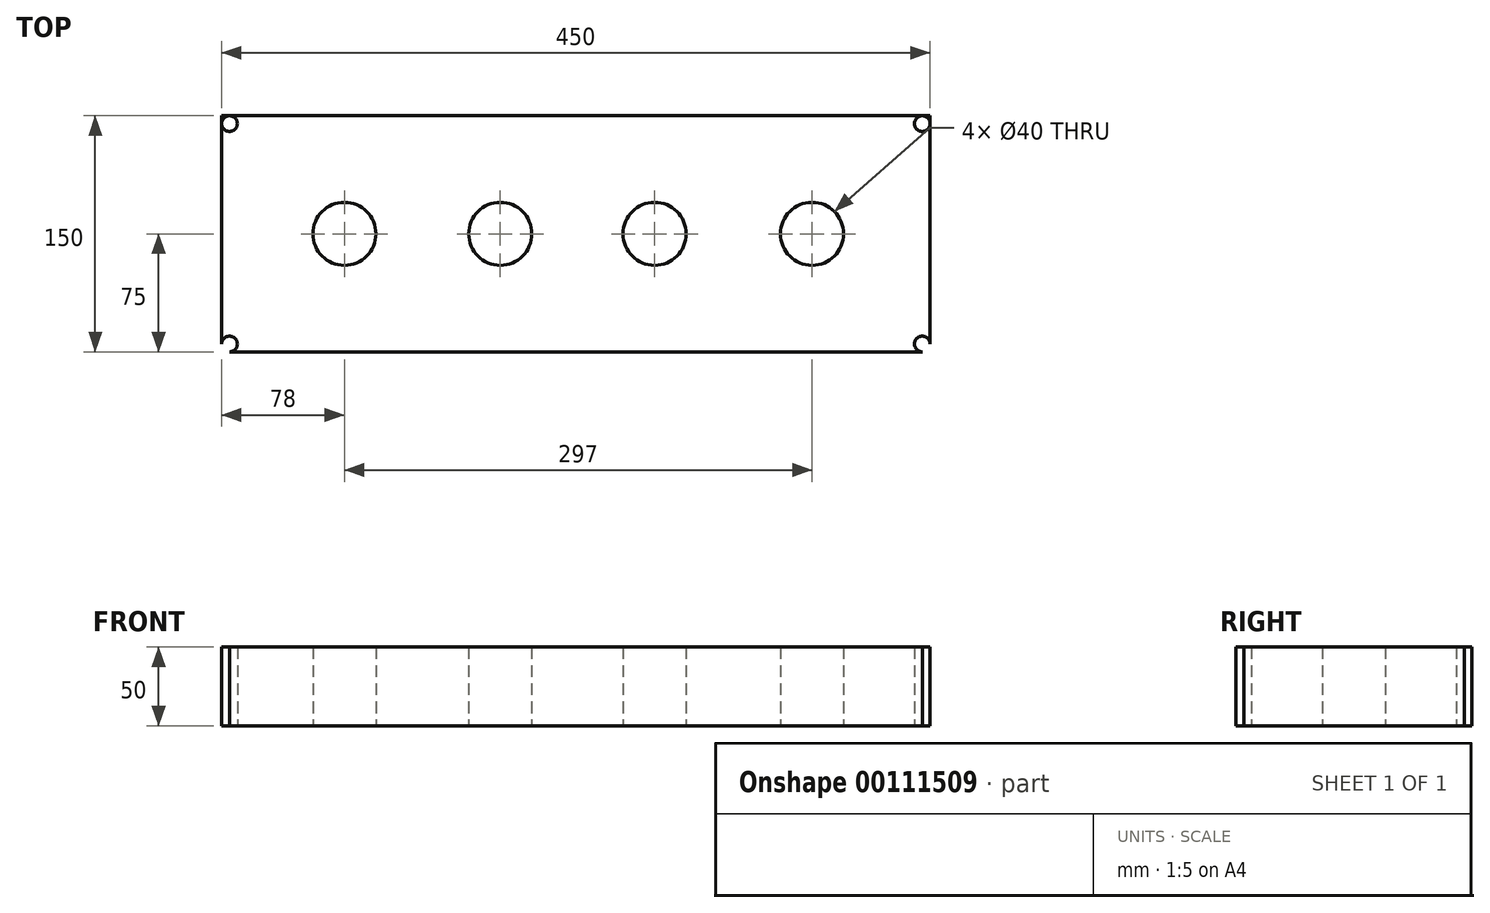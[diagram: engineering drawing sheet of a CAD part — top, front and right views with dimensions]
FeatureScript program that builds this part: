
annotation { "Feature Type Name" : "Feature", "Feature Type Description" : "" }
export const myFeature = defineFeature(function(context is Context, id is Id, definition is map)
    precondition{}
    {
        {
            var Q0;
            Q0=qCreatedBy(makeId("Top.planeOp"),FACE);
            var sketch = newSketch(context, id + "F0", { "sketchPlane" : qUnion([Q0])});
            skLineSegment(sketch, "E0.bottom", {"start": v(-225, 75) * mm, "end": v(225, 75) * mm});
            skLineSegment(sketch, "E0.top", {"start": v(-225, -75) * mm, "end": v(225, -75) * mm});
            skLineSegment(sketch, "E0.left", {"start": v(-225, 75) * mm, "end": v(-225, -75) * mm});
            skLineSegment(sketch, "E0.right", {"start": v(225, 75) * mm, "end": v(225, -75) * mm});
            skPoint(sketch, "E0.middle", {"position": v(0, 0) * mm});
            skPoint(sketch, "E1", {"position": v(-147, 0) * mm});
            skPoint(sketch, "E2", {"position": v(50, 0) * mm});
            skPoint(sketch, "E3", {"position": v(150, 0) * mm});
            skPoint(sketch, "E4", {"position": v(-48, 0) * mm});
            skCircle(sketch, "E5", {"center": v(-147, 0) * mm, "radius": 20 * mm});
            skCircle(sketch, "E6", {"center": v(-48, 0) * mm, "radius": 20 * mm});
            skCircle(sketch, "E7", {"center": v(150, 0) * mm, "radius": 20 * mm});
            skCircle(sketch, "E8", {"center": v(50, 0) * mm, "radius": 20 * mm});
            skCircle(sketch, "E9", {"center": v(-220, -70) * mm, "radius": 5 * mm});
            skCircle(sketch, "E10", {"center": v(220, 70) * mm, "radius": 5 * mm});
            skCircle(sketch, "E11", {"center": v(220, -70) * mm, "radius": 5 * mm});
            skPoint(sketch, "E12", {"position": v(-24.77, 40) * mm});
            skCircle(sketch, "E13", {"center": v(-220, 70) * mm, "radius": 5 * mm});
            skSolve(sketch);
        }
        {
            var Q0;
            Q0=makeQuery(id+"F0.imprint","IMPRINT",FACE,{"disambiguationData":[TD([[makeQuery(id+"F0.imprint","IMPRINT",EDGE,{"derivedFrom":sQuery(id+"F0.wireOp",EDGE,"E0.bottom")}),-1.0]])]});
            var Q1;
            Q1=makeQuery(id+"F0.imprint","IMPRINT",FACE,{"disambiguationData":[TD([[makeQuery(id+"F0.imprint","IMPRINT",EDGE,{"derivedFrom":sQuery(id+"F0.wireOp",EDGE,"E5")}),-1.0]])]});
            extrude(context, id + "F1", {"entities" : qUnion([Q0, Q1]), "depth" : 50 * mm});
        }
    });
